# Revit family: Mantis_Chair_BIM
name_source: partatom
category: Arredi
units: mm (PartAtom-declared; Revit-internal decimal feet)

## family parameters
Attiva taglio nelle viste = No
Basato su piano di lavoro = No
Condiviso = No
Numero OmniClass = 23.40.20.00
Origine composizione di rendering = Geometria famiglia
Punto di calcolo locali = No
Sempre verticale = Sì
Taglio con vuoti quando caricato = No
Titolo OmniClass = General Furniture and Specialties

## types (2) — shared parameters
AVAILABLE FINISHES = Ebonized black lacquer on Ash (EB) or bleached, white pigment, matte acrylic on Ash (BL). Raw effect lacquer on Oak (RE). Hand rubbed natural oil on Oak or Walnut (NA), or hand rubbed black oil on Walnut (BO).
BASE MATERIAL = BASSAM_FELLOWS_WALNUT_BLACK_OIL_W-BO
BIM BADGE = https://bim.archiproducts.com
COLLECTION = Mantis
DEPTH = 533 mm
HEIGHT = 775 mm
MATERIAL DESCRIPTION = Carved solid wood.
Modello = Mantis Chair
PILLOW MATERIAL = BASSAM_FELLOWS_COMFORT_LEATHER_43632_CAMEL
PRODUCT SHEET = https://www.archiproducts.com
Produttore = BassamFellows
STRUCTURE MATERIAL = BASSAM_FELLOWS_WALNUT_BLACK_OIL_W-BO
TECHNICAL SHEET = https://bassamfellows.com
UPHOLSTERY MATERIAL = <Per categoria>
URL = https://bassamfellows.com
WIDTH = 638 mm
zero-valued in all types: Prospetto di default

## per-type parameters (varying)
| type | Descrizione | PRODUCT CODE |
| CB-25 | Solid wood chair with armrests | CB-25 |
| CB-25_Cushion | Solid wood chair with armrests and leather cushion | CB-25_CB-205 |

## geometry (parser evidence)
native form markers: Sweep x1
no freeform markers — native parametric forms only
